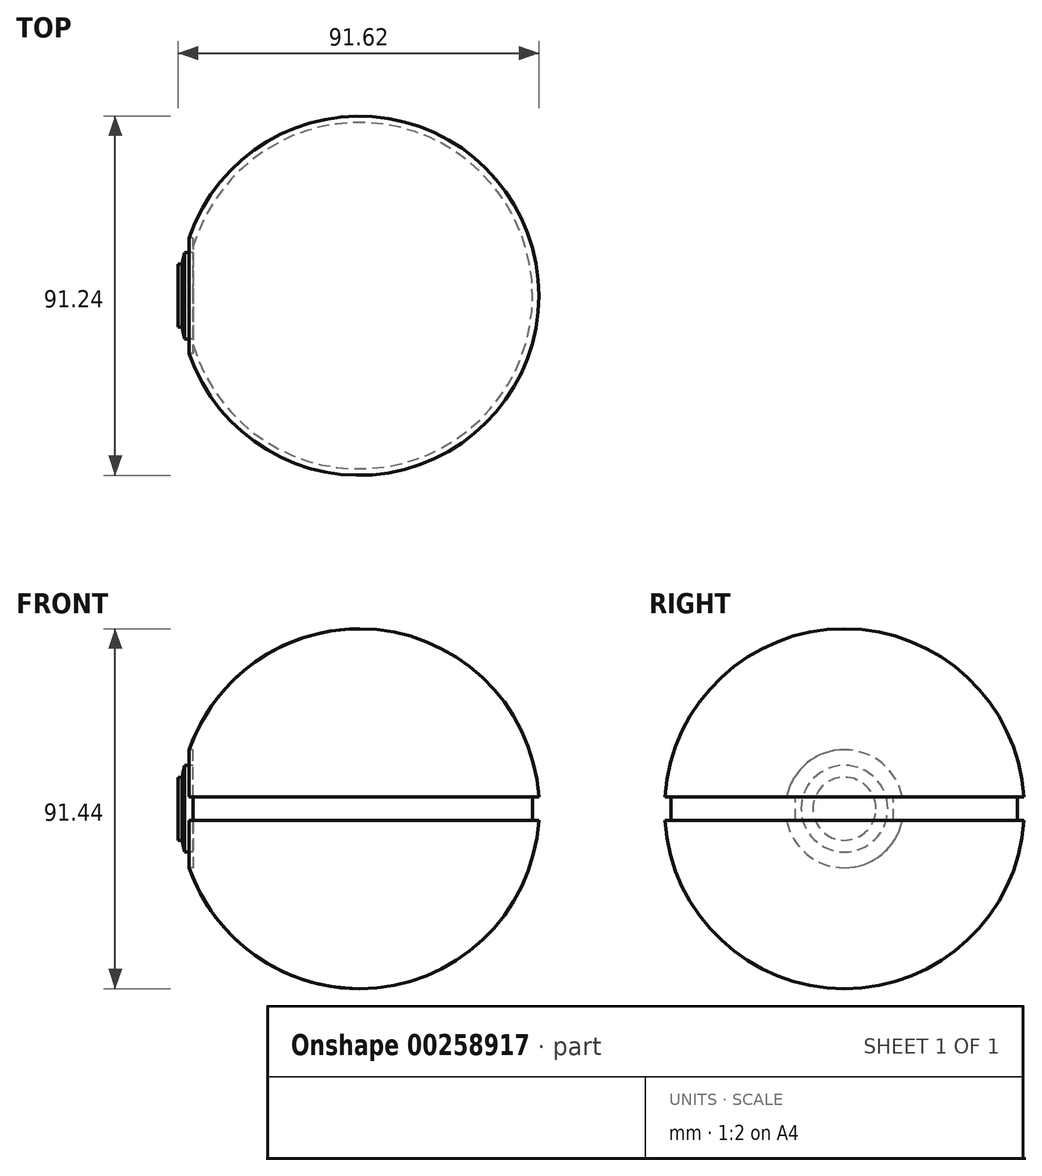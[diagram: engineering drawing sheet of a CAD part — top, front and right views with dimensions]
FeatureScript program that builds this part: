
annotation { "Feature Type Name" : "Feature", "Feature Type Description" : "" }
export const myFeature = defineFeature(function(context is Context, id is Id, definition is map)
    precondition{}
    {
        {
            var Q0;
            Q0=qCreatedBy(makeId("Front.planeOp"),FACE);
            var sketch = newSketch(context, id + "F0", { "sketchPlane" : qUnion([Q0])});
            skLineSegment(sketch, "E0", {"start": v(0, 0) * mm, "end": v(0, 45.72) * mm, "construction": true});
            skLineSegment(sketch, "E1", {"start": v(0, 0) * mm, "end": v(0, -45.72) * mm, "construction": true});
            skArc(sketch, "E2", {"start": v(0, -45.72) * mm, "mid": v(45.72, 0) * mm, "end": v(0, 45.72) * mm});
            skLineSegment(sketch, "E3", {"start": v(0, 45.72) * mm, "end": v(0, -45.72) * mm});
            skSolve(sketch);
        }
        {
            var Q0;
            Q0 = qSketchRegion(id + "F0", true);
            var Q1;
            Q1=sQuery(id+"F0.wireOp",EDGE,"E3");
            revolve(context, id + "F1", {"entities" : qUnion([Q0]), "axis" : qUnion([Q1]), "revolveType" : RevolveType.FULL});
        }
        {
            var Q0;
            Q0=qCreatedBy(makeId("Right.planeOp"),FACE);
            cPlane(context, id + "F2", {"entities" : qUnion([Q0]), "cplaneType" : CPlaneType.OFFSET, "offset" : 52.2 * mm, "oppositeDirection" : true, "width" : 150 * mm, "height" : 150 * mm});
        }
        {
            var Q0;
            Q0=qCreatedBy(id+"F2.planeOp",FACE);
            var sketch = newSketch(context, id + "F3", { "sketchPlane" : qUnion([Q0])});
            skCircle(sketch, "E4", {"center": v(0, 0) * mm, "radius": 11 * mm});
            skCircle(sketch, "E5", {"center": v(0, 0) * mm, "radius": 15 * mm});
            skSolve(sketch);
        }
        {
            var Q0;
            Q0 = qSketchRegion(id + "F3", true);
            extrude(context, id + "F4", {"entities" : qUnion([Q0]), "operationType" : NewBodyOperationType.REMOVE, "depth" : 10 * mm});
        }
        {
            var Q0;
            Q0=qCreatedBy(makeId("Front.planeOp"),FACE);
            var sketch = newSketch(context, id + "F5", { "sketchPlane" : qUnion([Q0])});
            skLineSegment(sketch, "E6", {"start": v(0, 67.93) * mm, "end": v(0, -73.6) * mm, "construction": true});
            skLineSegment(sketch, "E7.bottom", {"start": v(49.56, 3) * mm, "end": v(44, 3) * mm});
            skLineSegment(sketch, "E7.top", {"start": v(49.56, -3) * mm, "end": v(44, -3) * mm});
            skLineSegment(sketch, "E7.left", {"start": v(49.56, 3) * mm, "end": v(49.56, -3) * mm});
            skLineSegment(sketch, "E7.right", {"start": v(44, 3) * mm, "end": v(44, -3) * mm});
            skSolve(sketch);
        }
        {
            var Q0;
            Q0 = qSketchRegion(id + "F5", true);
            var Q1;
            Q1=sQuery(id+"F5.wireOp",EDGE,"E6");
            revolve(context, id + "F6", {"operationType" : NewBodyOperationType.REMOVE, "entities" : qUnion([Q0]), "axis" : qUnion([Q1]), "revolveType" : RevolveType.SYMMETRIC, "angle" : 330 * degree});
        }
        {
            var Q0;
            Q0=qCreatedBy(makeId("Front.planeOp"),FACE);
            var sketch = newSketch(context, id + "F7", { "sketchPlane" : qUnion([Q0])});
            skLineSegment(sketch, "E8", {"start": v(0, 0) * mm, "end": v(-113.6, 0) * mm, "construction": true});
            skLineSegment(sketch, "E9.bottom", {"start": v(-45, 8) * mm, "end": v(-46, 8) * mm});
            skLineSegment(sketch, "E9.top", {"start": v(-45, 0) * mm, "end": v(-46, 0) * mm});
            skLineSegment(sketch, "E9.left", {"start": v(-46, 8) * mm, "end": v(-46, 0) * mm});
            skLineSegment(sketch, "E9.right", {"start": v(-45, 8) * mm, "end": v(-45, 0) * mm});
            skSolve(sketch);
        }
        {
            var Q0;
            Q0 = qSketchRegion(id + "F7", true);
            var Q1;
            Q1=sQuery(id+"F7.wireOp",EDGE,"E8");
            revolve(context, id + "F8", {"operationType" : NewBodyOperationType.ADD, "entities" : qUnion([Q0]), "axis" : qUnion([Q1]), "revolveType" : RevolveType.FULL});
        }
    });
